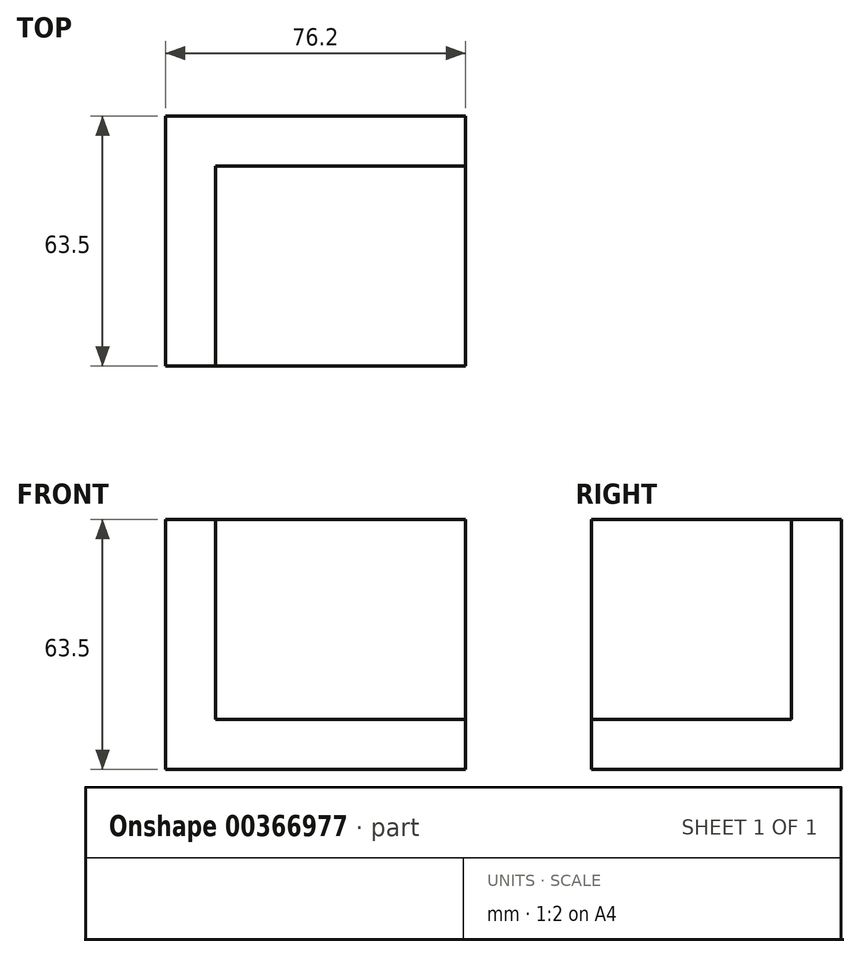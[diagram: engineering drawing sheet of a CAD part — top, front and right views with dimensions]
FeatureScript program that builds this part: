
annotation { "Feature Type Name" : "Feature", "Feature Type Description" : "" }
export const myFeature = defineFeature(function(context is Context, id is Id, definition is map)
    precondition{}
    {
        {
            var Q0;
            Q0=qCreatedBy(makeId("Front.planeOp"),FACE);
            var sketch = newSketch(context, id + "F0", { "sketchPlane" : qUnion([Q0])});
            skLineSegment(sketch, "E0.bottom", {"start": v(0, 0) * mm, "end": v(12.7, 0) * mm});
            skLineSegment(sketch, "E0.top", {"start": v(0, -63.5) * mm, "end": v(12.7, -63.5) * mm});
            skLineSegment(sketch, "E0.left", {"start": v(0, 0) * mm, "end": v(0, -63.5) * mm});
            skLineSegment(sketch, "E0.right", {"start": v(12.7, 0) * mm, "end": v(12.7, -63.5) * mm});
            skSolve(sketch);
        }
        {
            var Q0;
            Q0 = qSketchRegion(id + "F0", true);
            extrude(context, id + "F1", {"entities" : qUnion([Q0]), "depth" : 63.5 * mm});
        }
        {
            var Q0;
            Q0=makeQuery(id+"F1.opExtrude","SWEPT_FACE",FACE,{"disambiguationData":[OSD([sQuery(id+"F0.wireOp",EDGE,"E0.right")])]});
            extrude(context, id + "F2", {"entities" : qUnion([Q0]), "operationType" : NewBodyOperationType.ADD, "depth" : 63.5 * mm});
        }
        {
            var Q0;
            {var subQ0=sQuery(id+"F0.wireOp",EDGE,"E0.right");Q0=makeQuery(id+"F2.boolean.opBoolean","MERGE",FACE,{"derivedFrom":[makeQuery(id+"F1.opExtrude","CAP_FACE",FACE,{"disambiguationData":[OSD([sQuery(id+"F0.wireOp",EDGE,"E0.bottom"),sQuery(id+"F0.wireOp",EDGE,"E0.top"),sQuery(id+"F0.wireOp",EDGE,"E0.left"),subQ0])],"isStart":false}),makeQuery(id+"F2.opExtrude","SWEPT_FACE",FACE,{"disambiguationData":[OSD([subQ0]),TDD([makeQuery(id+"F1.opExtrude","CAP_EDGE",EDGE,{"disambiguationData":[OSD([subQ0])],"isStart":false})])]})]});}
            var Q1;
            {var subQ0=sQuery(id+"F0.wireOp",EDGE,"E0.bottom");Q1=makeQuery(id+"F2.boolean.opBoolean","MERGE",FACE,{"derivedFrom":[makeQuery(id+"F1.opExtrude","SWEPT_FACE",FACE,{"disambiguationData":[OSD([subQ0])]}),makeQuery(id+"F2.opExtrude","SWEPT_FACE",FACE,{"disambiguationData":[OSD([subQ0,sQuery(id+"F0.wireOp",EDGE,"E0.right")])]})]});}
            var Q2;
            Q2=makeQuery(id+"F2.opExtrude","CAP_FACE",FACE,{"disambiguationData":[OSD([sQuery(id+"F0.wireOp",EDGE,"E0.right")])],"isStart":false});
            shell(context, id + "F3", {"entities" : qUnion([Q0, Q1, Q2]), "thickness" : 12.7 * mm});
        }
    });
